# Revit family: HERZ Strömax Commissioning Valve With Integral Fixed orifice Plate 4017 M
name_source: partatom
category: Rohrzubehör
units: mm (PartAtom-declared; Revit-internal decimal feet)

## family parameters
Arbeitsebenenbasiert = Nein
Beim Laden mit Abzugskörper schneiden = Nein
Bemaßung runder Anschluss = Durchmesser verwenden
Gemeinsam genutzt = Nein
Immer vertikal = Ja
OmniClass-Nummer = 23.65.55.14
OmniClass-Titel = Valves for Liquid Services
Teiletyp = Unterbricht

## types (2) — shared parameters
Body = DZR brass
Field of application = Can be used as isolating and commissioning valve.
H02 = 13 mm
Hersteller = HERZ Armaturen Ges.m.b.H.
Max. differential pressure at closed valve = 1000000.0 Pa
Max. operating pressure = 2000000.0 Pa
Max. operating temperature = 130 °C
Medium = Water purity in accordance with the OeNORM H5195 and VDI 2035 standards.
Ethylene and propylene glycol can be mixed to a ratio of 25 - 50 vol. %.
Model = STRÖMAX 4017 M, commissioning valve in Y pattern with an orifice plate for differential pressure measurement, with test points:
DZR brass, female threaded ends, non-rising stem sealed with Triple-O-Ring, presetting through stroke limiting, handwhell with presetting digital display.
R01 = 12 mm  [stored 0.0393701 ft]
R02 = 9.5 mm  [stored 0.031168 ft]
R03 = 21.5 mm  [stored 0.0705381 ft]
S03 = 60 mm  [stored 0.19685 ft]
SCRNCODE = 05;07;02
SCRNSEQ = ARM;ARM_TYP="STRV";2
SW01 = 60.00°
URL = www.herzvalves.com
W01 = 50.00°
zero-valued in all types: E00, SC_NennweiteBerechnet, Vorgabe-Ansicht

## per-type parameters (varying)
| type | Insulation |
| without insulation | Nein |
| with insulation | Ja |

note: [stored X ft] marks values corroborated as IEEE doubles in the binary element streams (Revit-internal decimal feet)
